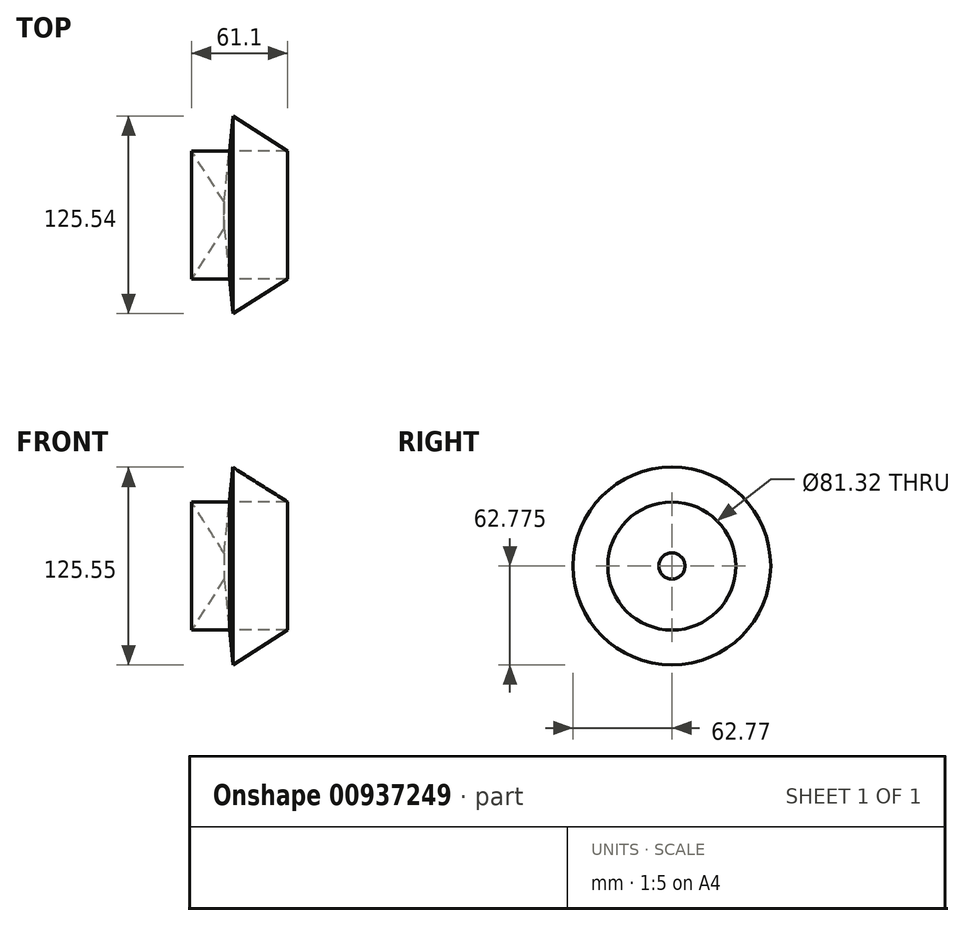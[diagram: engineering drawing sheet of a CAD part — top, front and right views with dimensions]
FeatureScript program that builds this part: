
annotation { "Feature Type Name" : "Feature", "Feature Type Description" : "" }
export const myFeature = defineFeature(function(context is Context, id is Id, definition is map)
    precondition{}
    {
        {
            var Q0;
            Q0=qCreatedBy(makeId("Front.planeOp"),FACE);
            var sketch = newSketch(context, id + "F0", { "sketchPlane" : qUnion([Q0])});
            skLineSegment(sketch, "E0", {"start": v(-26.27, 45.41) * mm, "end": v(34.83, 45.41) * mm});
            skLineSegment(sketch, "E1", {"start": v(34.83, 45.41) * mm, "end": v(0, 67.53) * mm});
            skLineSegment(sketch, "E2", {"start": v(0, 67.53) * mm, "end": v(-5.59, 13.08) * mm});
            skLineSegment(sketch, "E3", {"start": v(-26.27, 45.41) * mm, "end": v(-5.59, 13.08) * mm});
            skLineSegment(sketch, "E4", {"start": v(-15.93, 4.76) * mm, "end": v(31.03, 4.76) * mm});
            skPoint(sketch, "E4.startSnap0", {"position": v(-15.93, 29.25) * mm});
            skSolve(sketch);
        }
        {
            var Q0;
            Q0 = qSketchRegion(id + "F0", true);
            var Q1;
            Q1=sQuery(id+"F0.wireOp",EDGE,"E4");
            revolve(context, id + "F1", {"surfaceOperationType" : NewSurfaceOperationType.NEW, "entities" : qUnion([Q0]), "axis" : qUnion([Q1]), "revolveType" : RevolveType.FULL});
        }
    });
